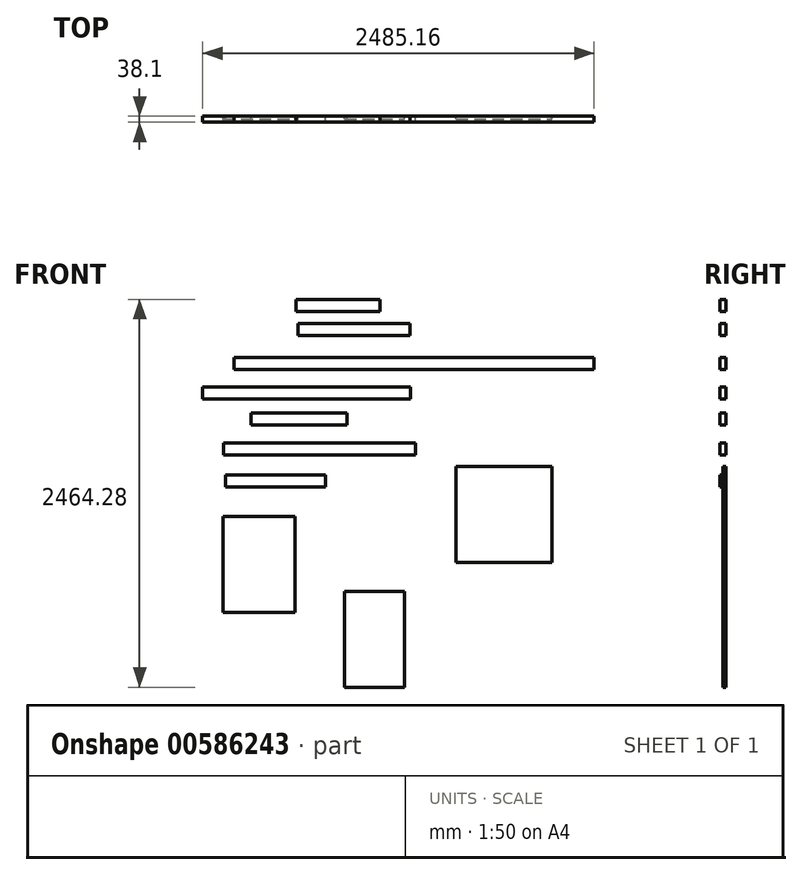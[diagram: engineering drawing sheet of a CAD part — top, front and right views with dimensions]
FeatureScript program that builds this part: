
annotation { "Feature Type Name" : "Feature", "Feature Type Description" : "" }
export const myFeature = defineFeature(function(context is Context, id is Id, definition is map)
    precondition{}
    {
        {
            var Q0;
            Q0=qCreatedBy(makeId("Front.planeOp"),FACE);
            var sketch = newSketch(context, id + "F0", { "sketchPlane" : qUnion([Q0])});
            skLineSegment(sketch, "E0", {"start": v(-1079.63, -37.7) * mm, "end": v(1206.37, -37.7) * mm});
            skLineSegment(sketch, "E1", {"start": v(1206.37, -37.7) * mm, "end": v(1206.37, -113.9) * mm});
            skLineSegment(sketch, "E2", {"start": v(1206.37, -113.9) * mm, "end": v(-1079.63, -113.9) * mm});
            skLineSegment(sketch, "E3", {"start": v(-1079.63, -113.9) * mm, "end": v(-1079.63, -37.7) * mm});
            skSolve(sketch);
        }
        {
            var Q0;
            Q0 = qSketchRegion(id + "F0", true);
            extrude(context, id + "F1", {"entities" : qUnion([Q0]), "depth" : 38.1 * mm, "offsetDistance" : 25.4 * mm});
        }
        {
            var Q0;
            Q0=qCreatedBy(makeId("Front.planeOp"),FACE);
            var sketch = newSketch(context, id + "F2", { "sketchPlane" : qUnion([Q0])});
            skLineSegment(sketch, "E4", {"start": v(-686.18, 333.3) * mm, "end": v(-152.78, 333.3) * mm});
            skLineSegment(sketch, "E5", {"start": v(-152.78, 333.3) * mm, "end": v(-152.78, 257.1) * mm});
            skLineSegment(sketch, "E6", {"start": v(-152.78, 257.1) * mm, "end": v(-686.18, 257.1) * mm});
            skLineSegment(sketch, "E7", {"start": v(-686.18, 257.1) * mm, "end": v(-686.18, 333.3) * mm});
            skSolve(sketch);
        }
        {
            var Q0;
            Q0 = qSketchRegion(id + "F2", true);
            extrude(context, id + "F3", {"entities" : qUnion([Q0]), "depth" : 38.1 * mm, "offsetDistance" : 25.4 * mm});
        }
        {
            var Q0;
            Q0=qCreatedBy(makeId("Front.planeOp"),FACE);
            var sketch = newSketch(context, id + "F4", { "sketchPlane" : qUnion([Q0])});
            skLineSegment(sketch, "E8", {"start": v(-674.5, 178.85) * mm, "end": v(36.7, 178.85) * mm});
            skLineSegment(sketch, "E9", {"start": v(36.7, 178.85) * mm, "end": v(36.7, 102.65) * mm});
            skLineSegment(sketch, "E10", {"start": v(36.7, 102.65) * mm, "end": v(-674.5, 102.65) * mm});
            skLineSegment(sketch, "E11", {"start": v(-674.5, 102.65) * mm, "end": v(-674.5, 178.85) * mm});
            skSolve(sketch);
        }
        {
            var Q0;
            Q0 = qSketchRegion(id + "F4", true);
            extrude(context, id + "F5", {"entities" : qUnion([Q0]), "depth" : 38.1 * mm, "offsetDistance" : 25.4 * mm});
        }
        {
            var Q0;
            Q0=qCreatedBy(makeId("Front.planeOp"),FACE);
            var sketch = newSketch(context, id + "F6", { "sketchPlane" : qUnion([Q0])});
            skLineSegment(sketch, "E12", {"start": v(-1278.79, -223.35) * mm, "end": v(42.01, -223.35) * mm});
            skLineSegment(sketch, "E13", {"start": v(42.01, -223.35) * mm, "end": v(42.01, -299.55) * mm});
            skLineSegment(sketch, "E14", {"start": v(42.01, -299.55) * mm, "end": v(-1278.79, -299.55) * mm});
            skLineSegment(sketch, "E15", {"start": v(-1278.79, -299.55) * mm, "end": v(-1278.79, -223.35) * mm});
            skSolve(sketch);
        }
        {
            var Q0;
            Q0 = qSketchRegion(id + "F6", true);
            extrude(context, id + "F7", {"entities" : qUnion([Q0]), "depth" : 38.1 * mm, "offsetDistance" : 25.4 * mm});
        }
        {
            var Q0;
            Q0=qCreatedBy(makeId("Front.planeOp"),FACE);
            var sketch = newSketch(context, id + "F8", { "sketchPlane" : qUnion([Q0])});
            skLineSegment(sketch, "E16", {"start": v(-533.4, -346.95) * mm, "end": v(0, -346.95) * mm});
            skLineSegment(sketch, "E17", {"start": v(0, -346.95) * mm, "end": v(0, -423.15) * mm});
            skLineSegment(sketch, "E18", {"start": v(0, -423.15) * mm, "end": v(-533.4, -423.15) * mm});
            skLineSegment(sketch, "E19", {"start": v(-533.4, -423.15) * mm, "end": v(-533.4, -346.95) * mm});
            skSolve(sketch);
        }
        {
            var Q0;
            Q0 = qSketchRegion(id + "F8", true);
            extrude(context, id + "F9", {"entities" : qUnion([Q0]), "depth" : 38.1 * mm, "offsetDistance" : 25.4 * mm});
        }
        {
            var Q0;
            Q0=qCreatedBy(makeId("Front.planeOp"),FACE);
            var sketch = newSketch(context, id + "F10", { "sketchPlane" : qUnion([Q0])});
            skLineSegment(sketch, "E20", {"start": v(-1146.6, -577.72) * mm, "end": v(72.6, -577.72) * mm});
            skLineSegment(sketch, "E21", {"start": v(72.6, -577.72) * mm, "end": v(72.6, -653.92) * mm});
            skLineSegment(sketch, "E22", {"start": v(72.6, -653.92) * mm, "end": v(-1146.6, -653.92) * mm});
            skLineSegment(sketch, "E23", {"start": v(-1146.6, -653.92) * mm, "end": v(-1146.6, -577.72) * mm});
            skSolve(sketch);
        }
        {
            var Q0;
            Q0 = qSketchRegion(id + "F10", true);
            extrude(context, id + "F11", {"entities" : qUnion([Q0]), "depth" : 38.1 * mm, "offsetDistance" : 25.4 * mm});
        }
        {
            var Q0;
            Q0=makeQuery(id+"F9.opExtrude","SWEPT_BODY",BODY,{"disambiguationData":[OSD([sQuery(id+"F8.wireOp",EDGE,"E16"),sQuery(id+"F8.wireOp",EDGE,"E17"),sQuery(id+"F8.wireOp",EDGE,"E18"),sQuery(id+"F8.wireOp",EDGE,"E19")])]});
            deleteBodies(context, id + "F12", {"entities" : qUnion([Q0])});
        }
        {
            var Q0;
            Q0=qCreatedBy(makeId("Front.planeOp"),FACE);
            var sketch = newSketch(context, id + "F13", { "sketchPlane" : qUnion([Q0])});
            skLineSegment(sketch, "E24", {"start": v(-972.12, -387.6) * mm, "end": v(-362.52, -387.6) * mm});
            skLineSegment(sketch, "E25", {"start": v(-362.52, -387.6) * mm, "end": v(-362.52, -463.8) * mm});
            skLineSegment(sketch, "E26", {"start": v(-362.52, -463.8) * mm, "end": v(-972.12, -463.8) * mm});
            skLineSegment(sketch, "E27", {"start": v(-972.12, -463.8) * mm, "end": v(-972.12, -387.6) * mm});
            skSolve(sketch);
        }
        {
            var Q0;
            Q0 = qSketchRegion(id + "F13", true);
            extrude(context, id + "F14", {"entities" : qUnion([Q0]), "depth" : 38.1 * mm, "offsetDistance" : 25.4 * mm});
        }
        {
            var Q0;
            Q0=qCreatedBy(makeId("Front.planeOp"),FACE);
            var sketch = newSketch(context, id + "F15", { "sketchPlane" : qUnion([Q0])});
            skLineSegment(sketch, "E28", {"start": v(-1135.02, -782.54) * mm, "end": v(-500.02, -782.54) * mm});
            skLineSegment(sketch, "E29", {"start": v(-500.02, -782.54) * mm, "end": v(-500.02, -858.74) * mm});
            skLineSegment(sketch, "E30", {"start": v(-500.02, -858.74) * mm, "end": v(-1135.02, -858.74) * mm});
            skLineSegment(sketch, "E31", {"start": v(-1135.02, -858.74) * mm, "end": v(-1135.02, -782.54) * mm});
            skSolve(sketch);
        }
        {
            var Q0;
            Q0 = qSketchRegion(id + "F15", true);
            extrude(context, id + "F16", {"entities" : qUnion([Q0]), "depth" : 38.1 * mm, "offsetDistance" : 25.4 * mm});
        }
        {
            var Q0;
            Q0=qCreatedBy(makeId("Front.planeOp"),FACE);
            var sketch = newSketch(context, id + "F17", { "sketchPlane" : qUnion([Q0])});
            skLineSegment(sketch, "E32", {"start": v(331.07, -728.92) * mm, "end": v(940.67, -728.92) * mm});
            skLineSegment(sketch, "E33", {"start": v(940.67, -728.92) * mm, "end": v(940.67, -1338.52) * mm});
            skLineSegment(sketch, "E34", {"start": v(940.67, -1338.52) * mm, "end": v(331.07, -1338.52) * mm});
            skLineSegment(sketch, "E35", {"start": v(331.07, -1338.52) * mm, "end": v(331.07, -728.92) * mm});
            skSolve(sketch);
        }
        {
            var Q0;
            Q0 = qSketchRegion(id + "F17", true);
            extrude(context, id + "F18", {"entities" : qUnion([Q0]), "depth" : 19.05 * mm, "offsetDistance" : 25.4 * mm});
        }
        {
            var Q0;
            Q0=qCreatedBy(makeId("Front.planeOp"),FACE);
            var sketch = newSketch(context, id + "F19", { "sketchPlane" : qUnion([Q0])});
            skLineSegment(sketch, "E36", {"start": v(-1148.91, -1045.13) * mm, "end": v(-691.71, -1045.13) * mm});
            skLineSegment(sketch, "E37", {"start": v(-691.71, -1045.13) * mm, "end": v(-691.71, -1654.73) * mm});
            skLineSegment(sketch, "E38", {"start": v(-691.71, -1654.73) * mm, "end": v(-1148.91, -1654.73) * mm});
            skLineSegment(sketch, "E39", {"start": v(-1148.91, -1654.73) * mm, "end": v(-1148.91, -1045.13) * mm});
            skSolve(sketch);
        }
        {
            var Q0;
            Q0 = qSketchRegion(id + "F19", true);
            extrude(context, id + "F20", {"entities" : qUnion([Q0]), "depth" : 19.05 * mm, "offsetDistance" : 25.4 * mm});
        }
        {
            var Q0;
            Q0=qCreatedBy(makeId("Front.planeOp"),FACE);
            var sketch = newSketch(context, id + "F21", { "sketchPlane" : qUnion([Q0])});
            skLineSegment(sketch, "E40", {"start": v(-377.67, -1521.38) * mm, "end": v(3.33, -1521.38) * mm});
            skLineSegment(sketch, "E41", {"start": v(3.33, -1521.38) * mm, "end": v(3.33, -2130.98) * mm});
            skLineSegment(sketch, "E42", {"start": v(3.33, -2130.98) * mm, "end": v(-377.67, -2130.98) * mm});
            skLineSegment(sketch, "E43", {"start": v(-377.67, -2130.98) * mm, "end": v(-377.67, -1521.38) * mm});
            skSolve(sketch);
        }
        {
            var Q0;
            Q0 = qSketchRegion(id + "F21", true);
            extrude(context, id + "F22", {"entities" : qUnion([Q0]), "depth" : 19.05 * mm, "offsetDistance" : 25.4 * mm});
        }
    });
